# Revit family: 90-6376-14-14
name_source: partatom
category: Luminarias
revit_build: Autodesk Revit 2017 (Build: 20160225_1515(x64)
units: mm (PartAtom-declared; Revit-internal decimal feet)

## family parameters
Anfitrión = Cara
Compartido = Sí
Corte con vacíos al cargar = No
Cota de conector redondo = Diámetro de uso
Número OmniClass = 23.80.70.00
Origen de luz = No
Punto de cálculo de habitación = No
Tipo de pieza = Normal
Título OmniClass = Lighting

## types (1)
- 90-6376-14-14
    Acabado = Blanco, Negro
    CRI = 90
    Carga aparente = 0 VA
    Catálogo = Technical
    CodigoGubimclass = 50.60.50.20
    CodigoOmniclass = 21-04 50 40
    CodigoUniclass2015 = EF_70_80
    CodigoUniformat2010 = D5040
    DescripcionGubimclass = Iluminación interior
    DescripcionOmniclass = Lighting
    DescripcionUniclass2015 = Lighting
    DescripcionUniformat2010 = Lighting
    EAN13 = 8435526843954
    Eficiencia energética = LED A++
    Elevación por defecto = 1000 mm  [stored 3.28084 ft]
    Etiqueta V/f = max. 700mA
    Fabricante = LEDS C4
    Familia = Bento Standard 12 LEDS Trim
    FechaVersion = Julio 2020
    Ficha = http://files.leds-c4.com
    Fotometría = http://files.leds-c4.com
    Fuente de luz = 12xLED 26.4 1520.00 lm
    IMC = http://files.leds-c4.com
    IP = IP23
    IfcExportAs = IfcLightFixture
IfcLightFixture
    IfcExportType = NOTDEFINED
    Imagen web = http://files.leds-c4.com
    LDT = http://files.leds-c4.com
    Lumenes reales (lm) = 1459
    Material = Aluminio, Policarbonato
    Peso neto (KG) = 0.39
    Pluma comercial = http://files.leds-c4.com
    Producto descatalogado = Catalogado ES
    Referencia = 90-6376-14-14
    Temperatura color led (K) = Blanco cálido - 2700K
    Tender text (Castellano) = LEDS C4
Bento Standard 12 LEDS Trim
90-6376-14-14

Luminària de techo de uso interior para iluminar hacia abajo. 

UGR &lt;10. Alto confort visual con efecto de lámpara invisible. Material estructura: Aluminio, Policarbonato. Acabado estructura: Blanco, Negro. Garantía: 5 Años.

Peso neto del producto (Kg): 0.390
Longitud del producto (mm): 332
Anchura o diámetro del producto (mm): 46
Altura del producto (mm): 50
Ø del agujero para empotrar (mm): 40x328
Grosor de techo admitido: 0-18

Clase 3. Luminaria no apta para ser recubierta con materiales aislantes. IP: IP23. LED. Nº de portalámparas o Leds: 12. Marca del LED: CREE. Potencia máxima de la fuente de luz: 26.4W. Temperatura de color: Blanco cálido - 2700K. Índice de reproducción cromática: 90. Steps Mac Adam: 3. Diámetro máximo de la bombilla que admite la luminaria: 50.000h L80B20. Riesgo fotobiológico: RG2. Flujo real (lm): 1459. Flujo nominal (lm): 1520. Lm/W reales: 55. Voltaje: 3. Equipo incluido: No, pero lo necesita. Potencia total: 26.4.
    Tender text (English) = LEDS C4
Bento Standard 12 LEDS Trim
90-6376-14-14

Downlight for indoor use. 

For downlighting. UGR &lt;10. Maximum visual comfort with invisible lamp effect. Structure material: Aluminium, Polycarbonate. Structure finish: White, Black. Warranty: 5 Years.

Product net weight (Kg): 0.390
Product length (mm): 332
Product width or diameter (mm): 46
Product height (mm): 50
Ø of the hole for recessing (mm): 40x328
Permitted ceiling thickness: 0-18

Class 3. Luminaire not suitable for coating with insulation materials. IP: IP23. LED. No. of lampholders or LEDs: 12. LED brand: CREE. Maximum power of light source: 26.4W. Colour temperature: LED warm-white 2700K. Colour rendering index: 90. MacAdam Steps: 3. Maximum diameter of luminaire bulb: 50.000h L80B20. Photobiological risk: RG2. Real flux (lm): 1459. Nominal flux (lm): 1520. Lm/Real W: 55. Voltage: 3. Gear included: No, but it is needed. Total power: 26.4.
    Tipo = Downlight
    Vatios (W) = 26.4
    Versión = v1

note: [stored X ft] marks values corroborated as IEEE doubles in the binary element streams (Revit-internal decimal feet)
